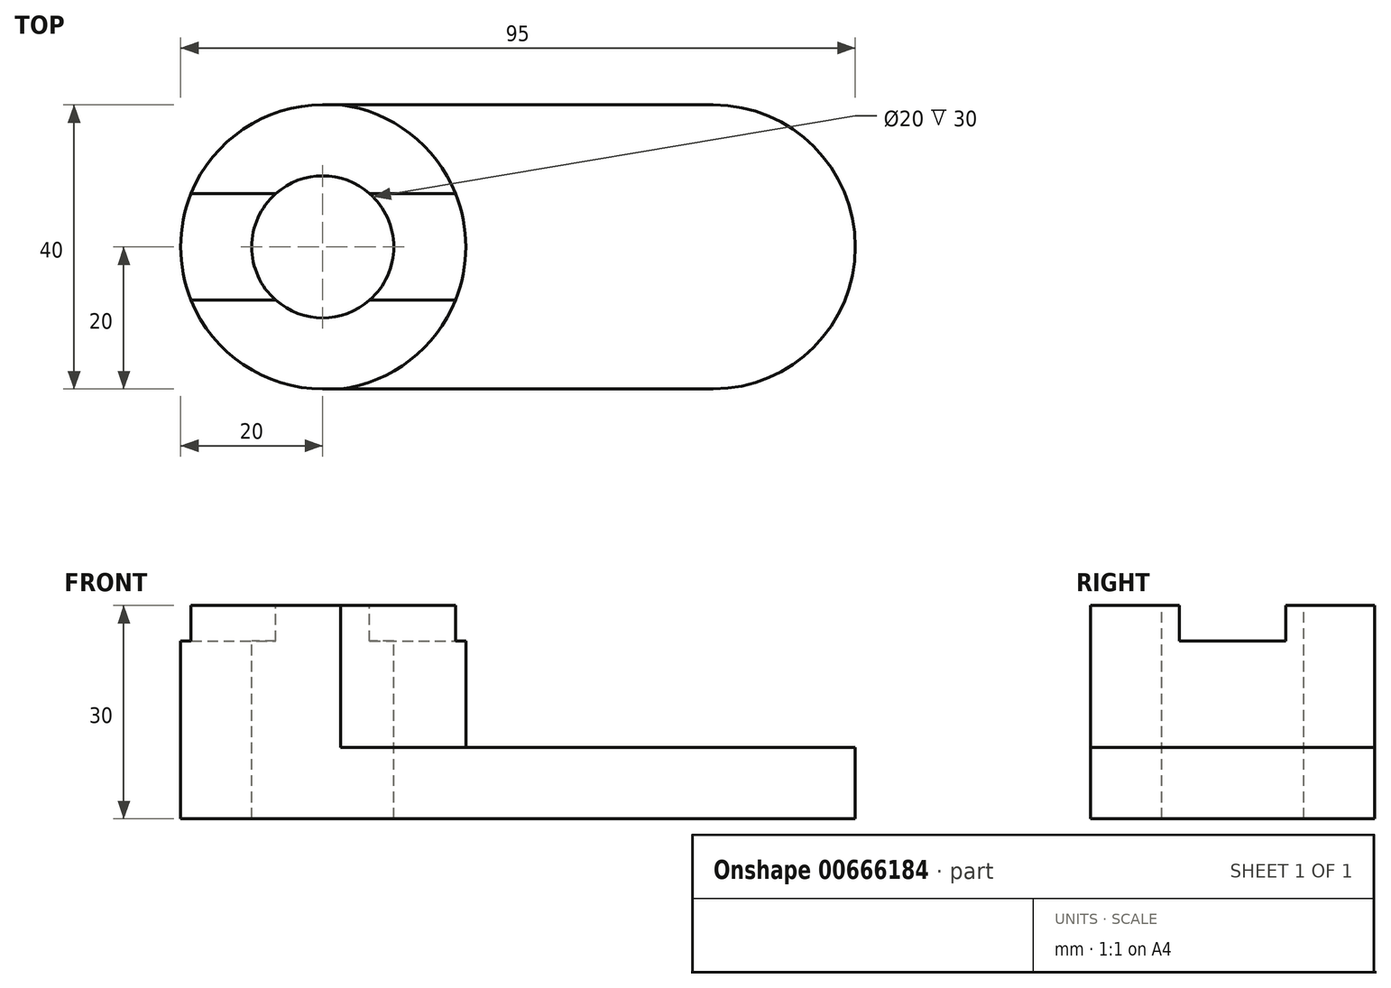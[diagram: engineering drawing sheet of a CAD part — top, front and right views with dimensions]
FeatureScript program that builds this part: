
annotation { "Feature Type Name" : "Feature", "Feature Type Description" : "" }
export const myFeature = defineFeature(function(context is Context, id is Id, definition is map)
    precondition{}
    {
        {
            var Q0;
            Q0=qCreatedBy(makeId("Top.planeOp"),FACE);
            var sketch = newSketch(context, id + "F0", { "sketchPlane" : qUnion([Q0])});
            skArc(sketch, "E0", {"start": v(0, 20) * mm, "mid": v(-20, 0) * mm, "end": v(0, -20) * mm});
            skArc(sketch, "E1", {"start": v(55, -20) * mm, "mid": v(75, 0) * mm, "end": v(55, 20) * mm});
            skLineSegment(sketch, "E2", {"start": v(0, 20) * mm, "end": v(55, 20) * mm});
            skLineSegment(sketch, "E3", {"start": v(0, -20) * mm, "end": v(55, -20) * mm});
            skSolve(sketch);
        }
        {
            var Q0;
            Q0=makeQuery(id+"F0.imprint","IMPRINT",FACE,{"disambiguationData":[TD([[makeQuery(id+"F0.imprint","IMPRINT",EDGE,{"derivedFrom":sQuery(id+"F0.wireOp",EDGE,"E0")}),1.0]])]});
            extrude(context, id + "F1", {"entities" : qUnion([Q0]), "depth" : 10 * mm, "offsetDistance" : 25 * mm});
        }
        {
            var Q0;
            Q0=makeQuery(id+"F1.opExtrude","CAP_FACE",FACE,{"disambiguationData":[OSD([sQuery(id+"F0.wireOp",EDGE,"E0"),sQuery(id+"F0.wireOp",EDGE,"E1"),sQuery(id+"F0.wireOp",EDGE,"E2"),sQuery(id+"F0.wireOp",EDGE,"E3")])],"isStart":false});
            var sketch = newSketch(context, id + "F2", { "sketchPlane" : qUnion([Q0])});
            skCircle(sketch, "E4", {"center": v(0, 0) * mm, "radius": 20.16 * mm});
            skSolve(sketch);
        }
        {
            var Q0;
            {var subQ5=makeQuery(id+"F1.opExtrude","CAP_EDGE",EDGE,{"disambiguationData":[OSD([sQuery(id+"F0.wireOp",EDGE,"E0")])],"isStart":false});Q0=makeQuery(id+"F2.imprint","IMPRINT",FACE,{"disambiguationData":[TD([[makeQuery(id+"F2.imprint","IMPRINT",EDGE,{"derivedFrom":subQ5}),1.0]])]});}
            extrude(context, id + "F3", {"entities" : qUnion([Q0]), "operationType" : NewBodyOperationType.ADD, "depth" : 20 * mm, "offsetDistance" : 25 * mm});
        }
        {
            var Q0;
            Q0=makeQuery(id+"F3.opExtrude","CAP_FACE",FACE,{"disambiguationData":[OSD([sQuery(id+"F0.wireOp",EDGE,"E0"),sQuery(id+"F0.wireOp",EDGE,"E2"),sQuery(id+"F0.wireOp",EDGE,"E3"),sQuery(id+"F2.wireOp",EDGE,"E4")])],"isStart":false});
            var sketch = newSketch(context, id + "F4", { "sketchPlane" : qUnion([Q0])});
            skCircle(sketch, "E5", {"center": v(0, 0) * mm, "radius": 10 * mm});
            skSolve(sketch);
        }
        {
            var Q0;
            Q0=makeQuery(id+"F4.imprint","IMPRINT",FACE,{"disambiguationData":[TD([[makeQuery(id+"F4.imprint","IMPRINT",EDGE,{"derivedFrom":sQuery(id+"F4.wireOp",EDGE,"E5")}),1.0]])]});
            extrude(context, id + "F5", {"entities" : qUnion([Q0]), "operationType" : NewBodyOperationType.REMOVE, "endBound" : BoundingType.THROUGH_ALL, "oppositeDirection" : true, "depth" : -25 * mm, "offsetDistance" : 25 * mm});
        }
        {
            var Q0;
            Q0=makeQuery(id+"F3.opExtrude","CAP_FACE",FACE,{"disambiguationData":[OSD([sQuery(id+"F0.wireOp",EDGE,"E0"),sQuery(id+"F0.wireOp",EDGE,"E2"),sQuery(id+"F0.wireOp",EDGE,"E3"),sQuery(id+"F2.wireOp",EDGE,"E4")])],"isStart":false});
            var sketch = newSketch(context, id + "F6", { "sketchPlane" : qUnion([Q0])});
            skLineSegment(sketch, "E6", {"start": v(-18.54, 7.5) * mm, "end": v(18.7, 7.5) * mm});
            skLineSegment(sketch, "E7", {"start": v(18.7, -7.5) * mm, "end": v(-18.54, -7.5) * mm});
            skSolve(sketch);
        }
        {
            var Q0;
            {var subQ0=sQuery(id+"F6.wireOp",EDGE,"E6");var subQ1=makeQuery(id+"F3.opExtrude","CAP_EDGE",EDGE,{"disambiguationData":[OSD([sQuery(id+"F0.wireOp",EDGE,"E0")])],"isStart":false});var subQ2=makeQuery(id+"F6.imprint","INTERSECT",VERTEX,{"derivedFrom":[subQ1,subQ0]});Q0=makeQuery(id+"F6.imprint","IMPRINT",FACE,{"disambiguationData":[TD([[makeQuery(id+"F6.imprint","IMPRINT",EDGE,{"disambiguationData":[TD([[subQ2,-1.0]])],"derivedFrom":subQ0}),-1.0]])]});}
            var Q1;
            {var subQ0=sQuery(id+"F6.wireOp",EDGE,"E6");var subQ1=makeQuery(id+"F3.opExtrude","CAP_EDGE",EDGE,{"disambiguationData":[OSD([sQuery(id+"F2.wireOp",EDGE,"E4")])],"isStart":false});var subQ2=makeQuery(id+"F6.imprint","INTERSECT",VERTEX,{"derivedFrom":[subQ1,subQ0]});Q1=makeQuery(id+"F6.imprint","IMPRINT",FACE,{"disambiguationData":[TD([[makeQuery(id+"F6.imprint","IMPRINT",EDGE,{"disambiguationData":[TD([[subQ2,1.0]])],"derivedFrom":subQ0}),-1.0]])]});}
            extrude(context, id + "F7", {"entities" : qUnion([Q0, Q1]), "operationType" : NewBodyOperationType.REMOVE, "oppositeDirection" : true, "depth" : 5 * mm, "offsetDistance" : 25 * mm});
        }
    });
